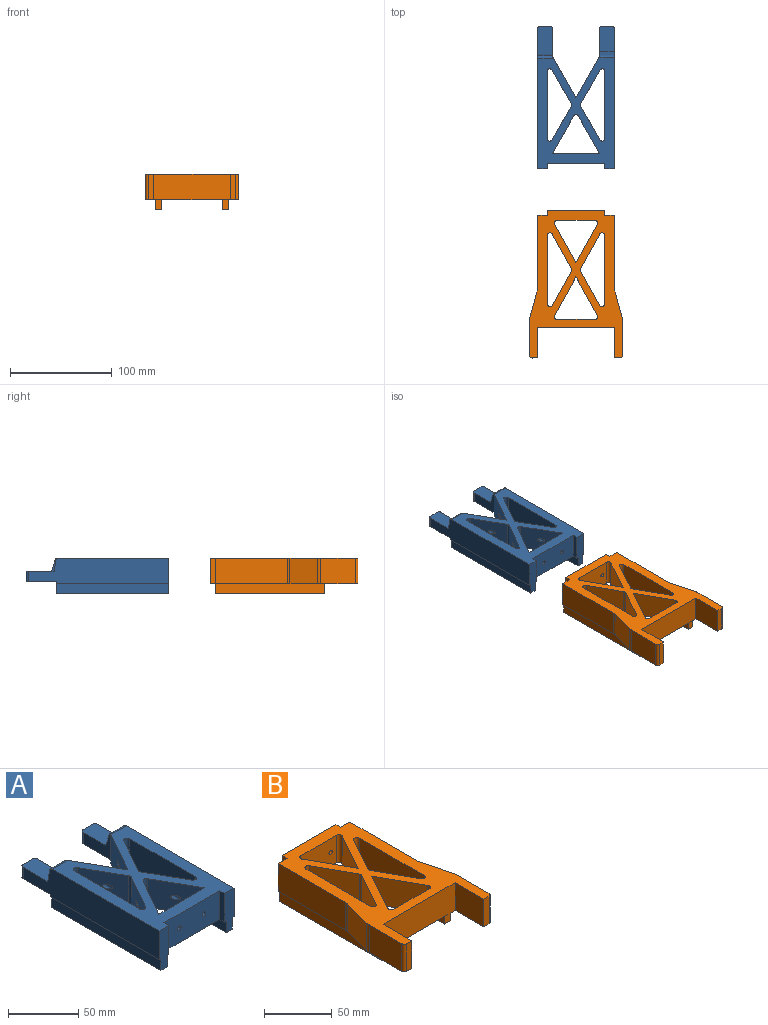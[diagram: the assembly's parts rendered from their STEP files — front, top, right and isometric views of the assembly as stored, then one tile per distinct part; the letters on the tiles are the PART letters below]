
ASSEMBLY  parts=2 mates=1
PART A: 59 faces, bbox 75.2x140x35 mm
  f0: plane 14.5x12mm, normal (0,1,0), area 93mm2, adj f2,f7,f8,f23,f30,f31,f32,f36
  f1: plane 110x1.55mm, normal (0,0,-1), area 170.5mm2, adj f10,f11,f21,f34
  f2: plane 110x59.3mm, normal (0,0,-1), area 2377.7mm2, adj f0,f3,f4,f5,f6,f8,f9,f10
  f3: plane 25x5mm, normal (1,0,0), area 125mm2, adj f2,f4,f21,f22
  f4: plane 56.2x25mm, normal (0,-1,0), area 1385mm2, adj f2,f3,f5,f22,f27,f28
  f5: plane 25x5mm, normal (-1,0,0), area 125mm2, adj f2,f4,f6,f22
  f6: plane 35x9.5mm, normal (0,-1,0), area 301.5mm2, adj f2,f5,f7,f22,f23,f30,f31,f32
  f7: plane 137.5x25mm, normal (1,0,0), area 3061.2mm2, adj f0,f6,f22,f23,f36,f38,f51,f54
  f8: plane 40.62x25.02mm, normal (-0.87,0.49,0), area 1147.5mm2, adj f0,f2,f9,f22,f29,f37,f54
  f9: plane 40.61x25mm, normal (0.87,0.49,0), area 1147.2mm2, adj f2,f8,f10,f22,f24,f42,f53
  f10: plane 14.5x12mm, normal (0,1,0), area 93mm2, adj f1,f2,f9,f11,f33,f34,f35,f40
  f11: plane 137.5x25mm, normal (-1,0,0), area 3042.5mm2, adj f1,f10,f21,f22,f40,f41,f52,f53
  f12: plane 33.05x25mm, normal (0.87,0.49,0), area 930.3mm2, adj f2,f22,f25,f47,f48
  f13: plane 33.05x25mm, normal (0.87,-0.49,0), area 930.3mm2, adj f2,f22,f29,f48,f50
  f14: plane 46.2x25mm, normal (0,1,0), area 1135mm2, adj f2,f15,f19,f22,f27,f28
  f15: plane 36.79x25mm, normal (0.87,-0.49,0), area 1037.8mm2, adj f2,f14,f22,f26,f46
  f16: plane 33.05x25mm, normal (-0.87,0.49,0), area 930.3mm2, adj f2,f22,f26,f44,f45
  f17: plane 66.1x25mm, normal (1,0,0), area 1652.5mm2, adj f2,f22,f44,f49
  f18: plane 66.1x25mm, normal (-1,0,0), area 1652.5mm2, adj f2,f22,f47,f50
  f19: plane 36.79x25mm, normal (-0.87,-0.49,0), area 1037.8mm2, adj f2,f14,f22,f25,f46
  f20: plane 33.05x25mm, normal (-0.87,-0.49,0), area 930.3mm2, adj f2,f22,f24,f45,f49
  f21: plane 35x9.5mm, normal (0,-1,0), area 301.5mm2, adj f1,f2,f3,f11,f22,f33,f34,f35
  f22: plane 108.86x75.2mm, normal (0,0,1), area 4083.1mm2, adj f3,f4,f5,f6,f7,f8,f9,f11
  f23: plane 110x1.55mm, normal (0,0,-1), area 170.5mm2, adj f0,f6,f7,f30
  f24: cylinder r=1.78mm len=20.11mm, axis (0,-1,0), area 154.7mm2, adj f9,f20
  f25: cylinder r=1.78mm len=20.11mm, axis (0,-1,0), area 154.7mm2, adj f12,f19
  f26: cylinder r=1.78mm len=20.11mm, axis (0,-1,0), area 154.7mm2, adj f15,f16
  f27: cylinder r=1.78mm len=10mm, axis (0,-1,0), area 112.2mm2, adj f4,f14
  f28: cylinder r=1.78mm len=10mm, axis (0,-1,0), area 112.2mm2, adj f4,f14
  f29: cylinder r=1.78mm len=20.11mm, axis (0,-1,0), area 154.7mm2, adj f8,f13
  f30: plane 110x10mm, normal (1,0,0), area 1100mm2, adj f0,f6,f23,f32
  f31: plane 110x10mm, normal (-1,0,0), area 1100mm2, adj f0,f2,f6,f32
  f32: plane 110x6.4mm, normal (0,0,-1), area 704mm2, adj f0,f6,f30,f31
  f33: plane 110x10mm, normal (1,0,0), area 1100mm2, adj f2,f10,f21,f35
  f34: plane 110x10mm, normal (-1,0,0), area 1100mm2, adj f1,f10,f21,f35
  f35: plane 110x6.4mm, normal (0,0,-1), area 704mm2, adj f10,f21,f33,f34
  f36: plane 30x14.5mm, normal (0,0,-1), area 432.3mm2, adj f0,f7,f37,f39,f55,f56
  f37: plane 27.5x22.73mm, normal (-1,0,0), area 311.3mm2, adj f8,f36,f38,f51,f54,f55
  f38: plane 25x14.5mm, normal (0,0,1), area 359.8mm2, adj f7,f37,f39,f51,f55,f56
  f39: plane 10x9.5mm, normal (0,1,0), area 95mm2, adj f36,f38,f55,f56
  f40: plane 30x14.5mm, normal (0,0,-1), area 432.3mm2, adj f10,f11,f42,f43,f57,f58
  f41: plane 27.5x14.5mm, normal (0,0,1), area 396.1mm2, adj f11,f42,f43,f52,f57,f58
  f42: plane 27.5x22.25mm, normal (1,0,0), area 292.9mm2, adj f9,f40,f41,f52,f53,f58
  f43: plane 10x9.5mm, normal (0,1,0), area 95mm2, adj f40,f41,f57,f58
  f44: cylinder r=2.5mm len=25mm, axis (0,0,-1), area 164mm2, adj f2,f16,f17,f22
  f45: cylinder r=2.5mm len=25mm, axis (0,0,-1), area 64.7mm2, adj f2,f16,f20,f22
  f46: cylinder r=2.5mm len=25mm, axis (0,0,1), area 131.7mm2, adj f2,f15,f19,f22
  f47: cylinder r=2.5mm len=25mm, axis (0,0,-1), area 164mm2, adj f2,f12,f18,f22
  f48: cylinder r=2.5mm len=25mm, axis (0,0,1), area 64.7mm2, adj f2,f12,f13,f22
  f49: cylinder r=2.5mm len=25mm, axis (0,0,1), area 164mm2, adj f2,f17,f20,f22
  f50: cylinder r=2.5mm len=25mm, axis (0,0,-1), area 164mm2, adj f2,f13,f18,f22
  f51: plane 14.5x11.29mm, normal (0,0.95,0.32), area 172.6mm2, adj f7,f37,f38,f54
  f52: plane 14.5x10.91mm, normal (0,0.99,0.16), area 160.4mm2, adj f11,f41,f42,f53
  f53: cylinder r=2.5mm len=15.52mm, axis (-1,0,0), area 51.9mm2, adj f9,f11,f22,f42,f52
  f54: cylinder r=2.5mm len=15.15mm, axis (1,0,0), area 45.7mm2, adj f7,f8,f22,f37,f51
  f55: cylinder r=2.5mm len=10mm, axis (0,0,-1), area 39.3mm2, adj f36,f37,f38,f39
  f56: cylinder r=2.5mm len=10mm, axis (0,0,1), area 39.3mm2, adj f7,f36,f38,f39
  f57: cylinder r=2.5mm len=10mm, axis (0,0,-1), area 39.3mm2, adj f11,f40,f41,f43
  f58: cylinder r=2.5mm len=10mm, axis (0,0,1), area 39.3mm2, adj f40,f41,f42,f43
PART B: 56 faces, bbox 91.2x145x35 mm
  f0: plane 37.51x25mm, normal (0,1,0), area 937.8mm2, adj f26,f27,f44,f46
  f1: plane 37.78x25mm, normal (0.87,-0.48,0), area 1079.9mm2, adj f25,f26,f27,f44
  f2: plane 33.83x25mm, normal (0.87,-0.48,0), area 967.1mm2, adj f26,f27,f42,f47
  f3: plane 67.67x25mm, normal (-1,0,0), area 1691.7mm2, adj f26,f27,f42,f43
  f4: plane 37.51x25mm, normal (0,-1,0), area 917.8mm2, adj f26,f27,f28,f29,f40,f41
  f5: plane 37.78x25mm, normal (-0.87,0.48,0), area 1079.9mm2, adj f22,f26,f27,f40
  f6: plane 33.83x25mm, normal (-0.87,0.48,0), area 967.1mm2, adj f26,f27,f38,f45
  f7: plane 67.67x25mm, normal (1,0,0), area 1691.7mm2, adj f26,f27,f38,f39
  f8: plane 30x25mm, normal (1,0,0), area 750mm2, adj f9,f24,f26,f27
  f9: plane 75.2x25mm, normal (0,-1,0), area 1880mm2, adj f8,f10,f26,f27
  f10: plane 30x25mm, normal (-1,0,0), area 750mm2, adj f9,f11,f26,f27
  f11: plane 25x5.5mm, normal (0,-1,0), area 137.5mm2, adj f10,f26,f27,f37
  f12: plane 34.19x25mm, normal (1,0,0), area 854.7mm2, adj f26,f27,f35,f37
  f13: plane 70.69x25mm, normal (1,0,0), area 1767.2mm2, adj f14,f26,f27,f33
  f14: plane 35x9.6mm, normal (0,1,0), area 304mm2, adj f13,f15,f26,f27,f52,f53,f55
  f15: plane 25x5mm, normal (1,0,0), area 125mm2, adj f14,f16,f26,f27
  f16: plane 56x25mm, normal (0,1,0), area 1380mm2, adj f15,f17,f26,f27,f28,f29
  f17: plane 25x5mm, normal (-1,0,0), area 125mm2, adj f16,f18,f26,f27
  f18: plane 35x9.6mm, normal (0,1,0), area 304mm2, adj f17,f19,f26,f27,f48,f49,f51
  f19: plane 70.69x25mm, normal (-1,0,0), area 1767.2mm2, adj f18,f26,f27,f32
  f20: plane 34.19x25mm, normal (-1,0,0), area 854.7mm2, adj f26,f27,f34,f36
  f21: plane 33.83x25mm, normal (0.87,0.48,0), area 967.1mm2, adj f26,f27,f43,f47
  f22: plane 37.78x25mm, normal (0.87,0.48,0), area 1079.9mm2, adj f5,f26,f27,f41
  f23: plane 33.83x25mm, normal (-0.87,-0.48,0), area 967.1mm2, adj f26,f27,f39,f45
  f24: plane 25x5.5mm, normal (0,-1,0), area 137.5mm2, adj f8,f26,f27,f36
  f25: plane 37.78x25mm, normal (-0.87,-0.48,0), area 1079.9mm2, adj f1,f26,f27,f46
  f26: plane 145x91.2mm, normal (0,0,1), area 5471.6mm2, adj f0,f1,f2,f3,f4,f5,f6,f7
  f27: plane 145x91.2mm, normal (0,0,-1), area 4102mm2, adj f0,f1,f2,f3,f4,f5,f6,f7
  f28: cylinder r=1.78mm len=10mm, axis (0,1,0), area 112.2mm2, adj f4,f16
  f29: cylinder r=1.78mm len=10mm, axis (0,1,0), area 112.2mm2, adj f4,f16
  f30: plane 27.47x25mm, normal (0.97,0.26,0), area 710.7mm2, adj f26,f27,f33,f35
  f31: plane 27.47x25mm, normal (-0.97,0.26,0), area 710.7mm2, adj f26,f27,f32,f34
  f32: cylinder r=10mm len=25mm, axis (0,0,1), area 65.2mm2, adj f19,f26,f27,f31
  f33: cylinder r=10mm len=25mm, axis (0,0,1), area 65.2mm2, adj f13,f26,f27,f30
  f34: cylinder r=10mm len=25mm, axis (0,0,1), area 65.2mm2, adj f20,f26,f27,f31
  f35: cylinder r=10mm len=25mm, axis (0,0,-1), area 65.2mm2, adj f12,f26,f27,f30
  f36: cylinder r=2.5mm len=25mm, axis (0,0,-1), area 98.2mm2, adj f20,f24,f26,f27
  f37: cylinder r=2.5mm len=25mm, axis (0,0,-1), area 98.2mm2, adj f11,f12,f26,f27
  f38: cylinder r=2.5mm len=25mm, axis (0,0,-1), area 164.7mm2, adj f6,f7,f26,f27
  f39: cylinder r=2.5mm len=25mm, axis (0,0,-1), area 164.7mm2, adj f7,f23,f26,f27
  f40: cylinder r=2.5mm len=25mm, axis (0,0,1), area 129.8mm2, adj f4,f5,f26,f27
  f41: cylinder r=2.5mm len=25mm, axis (0,0,-1), area 129.8mm2, adj f4,f22,f26,f27
  f42: cylinder r=2.5mm len=25mm, axis (0,0,1), area 164.7mm2, adj f2,f3,f26,f27
  f43: cylinder r=2.5mm len=25mm, axis (0,0,-1), area 164.7mm2, adj f3,f21,f26,f27
  f44: cylinder r=2.5mm len=25mm, axis (0,0,1), area 129.8mm2, adj f0,f1,f26,f27
  f45: cylinder r=2.5mm len=25mm, axis (0,0,1), area 63.3mm2, adj f6,f23,f26,f27
  f46: cylinder r=2.5mm len=25mm, axis (0,0,1), area 129.8mm2, adj f0,f25,f26,f27
  f47: cylinder r=2.5mm len=25mm, axis (0,0,-1), area 63.3mm2, adj f2,f21,f26,f27
  f48: plane 107x10mm, normal (-1,0,0), area 1070mm2, adj f18,f27,f50,f51
  f49: plane 107x10mm, normal (1,0,0), area 1070mm2, adj f18,f27,f50,f51
  f50: plane 10x6.4mm, normal (0,-1,0), area 64mm2, adj f27,f48,f49,f51
  f51: plane 107x6.4mm, normal (0,0,-1), area 684.8mm2, adj f18,f48,f49,f50
  f52: plane 107x10mm, normal (-1,0,0), area 1070mm2, adj f14,f27,f54,f55
  f53: plane 107x10mm, normal (1,0,0), area 1070mm2, adj f14,f27,f54,f55
  f54: plane 10x6.4mm, normal (0,-1,0), area 64mm2, adj f27,f52,f53,f55
  f55: plane 107x6.4mm, normal (0,0,-1), area 684.8mm2, adj f14,f52,f53,f54
PLACE A t=(-45.21,-84.77,19.34)mm
PLACE B rot(axis=(0.17,-0.95,0.26),0deg) t=(-45.11,-109.11,19.34)mm
MATE slider A.f4 <-> B.f16  axis (0,-1,0) through (-55.89,-19.45,31.84)mm
